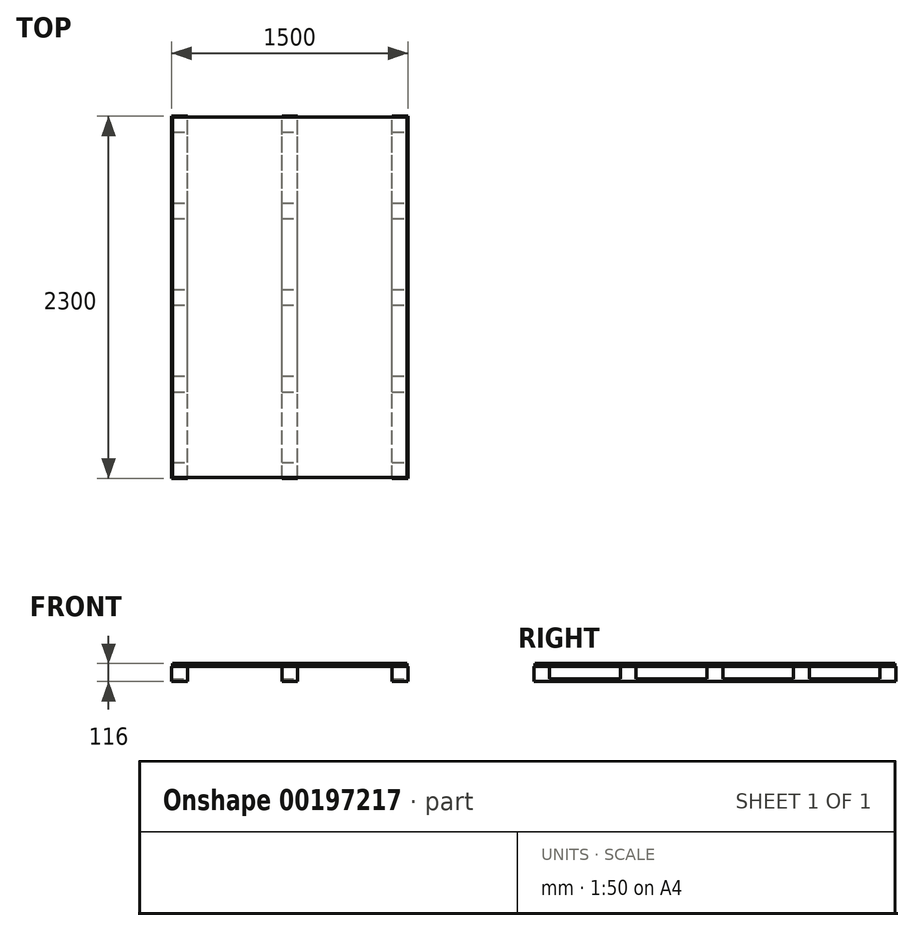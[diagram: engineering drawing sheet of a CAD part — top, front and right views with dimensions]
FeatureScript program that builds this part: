
annotation { "Feature Type Name" : "Feature", "Feature Type Description" : "" }
export const myFeature = defineFeature(function(context is Context, id is Id, definition is map)
    precondition{}
    {
        {
            var Q0;
            Q0=qCreatedBy(makeId("Top.planeOp"),FACE);
            var sketch = newSketch(context, id + "F0", { "sketchPlane" : qUnion([Q0])});
            skLineSegment(sketch, "E0.bottom", {"start": v(744, 1144) * mm, "end": v(-744, 1144) * mm});
            skLineSegment(sketch, "E0.top", {"start": v(744, -1144) * mm, "end": v(-744, -1144) * mm});
            skLineSegment(sketch, "E0.left", {"start": v(744, 1144) * mm, "end": v(744, -1144) * mm});
            skLineSegment(sketch, "E0.right", {"start": v(-744, 1144) * mm, "end": v(-744, -1144) * mm});
            skPoint(sketch, "E0.middle", {"position": v(0, 0) * mm});
            skSolve(sketch);
        }
        {
            var Q0;
            Q0=qSketchRegion(id+"F0",true);
            extrude(context, id + "F1", {"entities" : qUnion([Q0]), "depth" : 18 * mm});
        }
        {
            var Q0;
            Q0=makeQuery(id+"F1.opExtrude","CAP_FACE",FACE,{"disambiguationData":[OSD([sQuery(id+"F0.wireOp",EDGE,"E0.bottom"),sQuery(id+"F0.wireOp",EDGE,"E0.top"),sQuery(id+"F0.wireOp",EDGE,"E0.left"),sQuery(id+"F0.wireOp",EDGE,"E0.right")])],"isStart":true});
            var sketch = newSketch(context, id + "F2", { "sketchPlane" : qUnion([Q0])});
            skLineSegment(sketch, "E1.bottom", {"start": v(-750, 1150) * mm, "end": v(-650, 1150) * mm});
            skLineSegment(sketch, "E1.top", {"start": v(-750, 1050) * mm, "end": v(-650, 1050) * mm});
            skLineSegment(sketch, "E1.left", {"start": v(-750, 1150) * mm, "end": v(-750, 1050) * mm});
            skLineSegment(sketch, "E1.right", {"start": v(-650, 1150) * mm, "end": v(-650, 1050) * mm});
            skLineSegment(sketch, "E2.0.1.0", {"start": v(-750, 600) * mm, "end": v(-650, 600) * mm});
            skLineSegment(sketch, "E2.0.1.1", {"start": v(-650, 600) * mm, "end": v(-650, 500) * mm});
            skLineSegment(sketch, "E2.0.1.2", {"start": v(-750, 600) * mm, "end": v(-750, 500) * mm});
            skLineSegment(sketch, "E2.0.1.3", {"start": v(-750, 500) * mm, "end": v(-650, 500) * mm});
            skLineSegment(sketch, "E2.0.2.0", {"start": v(-750, 50) * mm, "end": v(-650, 50) * mm});
            skLineSegment(sketch, "E2.0.2.1", {"start": v(-650, 50) * mm, "end": v(-650, -50) * mm});
            skLineSegment(sketch, "E2.0.2.2", {"start": v(-750, 50) * mm, "end": v(-750, -50) * mm});
            skLineSegment(sketch, "E2.0.2.3", {"start": v(-750, -50) * mm, "end": v(-650, -50) * mm});
            skLineSegment(sketch, "E2.0.3.0", {"start": v(-750, -500) * mm, "end": v(-650, -500) * mm});
            skLineSegment(sketch, "E2.0.3.1", {"start": v(-650, -500) * mm, "end": v(-650, -600) * mm});
            skLineSegment(sketch, "E2.0.3.2", {"start": v(-750, -500) * mm, "end": v(-750, -600) * mm});
            skLineSegment(sketch, "E2.0.3.3", {"start": v(-750, -600) * mm, "end": v(-650, -600) * mm});
            skLineSegment(sketch, "E2.0.4.0", {"start": v(-750, -1050) * mm, "end": v(-650, -1050) * mm});
            skLineSegment(sketch, "E2.0.4.1", {"start": v(-650, -1050) * mm, "end": v(-650, -1150) * mm});
            skLineSegment(sketch, "E2.0.4.2", {"start": v(-750, -1050) * mm, "end": v(-750, -1150) * mm});
            skLineSegment(sketch, "E2.0.4.3", {"start": v(-750, -1150) * mm, "end": v(-650, -1150) * mm});
            skLineSegment(sketch, "E2.1.0.0", {"start": v(-50, 1150) * mm, "end": v(50, 1150) * mm});
            skLineSegment(sketch, "E2.1.0.1", {"start": v(50, 1150) * mm, "end": v(50, 1050) * mm});
            skLineSegment(sketch, "E2.1.0.2", {"start": v(-50, 1150) * mm, "end": v(-50, 1050) * mm});
            skLineSegment(sketch, "E2.1.0.3", {"start": v(-50, 1050) * mm, "end": v(50, 1050) * mm});
            skLineSegment(sketch, "E2.1.1.0", {"start": v(-50, 600) * mm, "end": v(50, 600) * mm});
            skLineSegment(sketch, "E2.1.1.1", {"start": v(50, 600) * mm, "end": v(50, 500) * mm});
            skLineSegment(sketch, "E2.1.1.2", {"start": v(-50, 600) * mm, "end": v(-50, 500) * mm});
            skLineSegment(sketch, "E2.1.1.3", {"start": v(-50, 500) * mm, "end": v(50, 500) * mm});
            skLineSegment(sketch, "E2.1.2.0", {"start": v(-50, 50) * mm, "end": v(50, 50) * mm});
            skLineSegment(sketch, "E2.1.2.1", {"start": v(50, 50) * mm, "end": v(50, -50) * mm});
            skLineSegment(sketch, "E2.1.2.2", {"start": v(-50, 50) * mm, "end": v(-50, -50) * mm});
            skLineSegment(sketch, "E2.1.2.3", {"start": v(-50, -50) * mm, "end": v(50, -50) * mm});
            skLineSegment(sketch, "E2.1.3.0", {"start": v(-50, -500) * mm, "end": v(50, -500) * mm});
            skLineSegment(sketch, "E2.1.3.1", {"start": v(50, -500) * mm, "end": v(50, -600) * mm});
            skLineSegment(sketch, "E2.1.3.2", {"start": v(-50, -500) * mm, "end": v(-50, -600) * mm});
            skLineSegment(sketch, "E2.1.3.3", {"start": v(-50, -600) * mm, "end": v(50, -600) * mm});
            skLineSegment(sketch, "E2.1.4.0", {"start": v(-50, -1050) * mm, "end": v(50, -1050) * mm});
            skLineSegment(sketch, "E2.1.4.1", {"start": v(50, -1050) * mm, "end": v(50, -1150) * mm});
            skLineSegment(sketch, "E2.1.4.2", {"start": v(-50, -1050) * mm, "end": v(-50, -1150) * mm});
            skLineSegment(sketch, "E2.1.4.3", {"start": v(-50, -1150) * mm, "end": v(50, -1150) * mm});
            skLineSegment(sketch, "E2.2.0.0", {"start": v(650, 1150) * mm, "end": v(750, 1150) * mm});
            skLineSegment(sketch, "E2.2.0.1", {"start": v(750, 1150) * mm, "end": v(750, 1050) * mm});
            skLineSegment(sketch, "E2.2.0.2", {"start": v(650, 1150) * mm, "end": v(650, 1050) * mm});
            skLineSegment(sketch, "E2.2.0.3", {"start": v(650, 1050) * mm, "end": v(750, 1050) * mm});
            skLineSegment(sketch, "E2.2.1.0", {"start": v(650, 600) * mm, "end": v(750, 600) * mm});
            skLineSegment(sketch, "E2.2.1.1", {"start": v(750, 600) * mm, "end": v(750, 500) * mm});
            skLineSegment(sketch, "E2.2.1.2", {"start": v(650, 600) * mm, "end": v(650, 500) * mm});
            skLineSegment(sketch, "E2.2.1.3", {"start": v(650, 500) * mm, "end": v(750, 500) * mm});
            skLineSegment(sketch, "E2.2.2.0", {"start": v(650, 50) * mm, "end": v(750, 50) * mm});
            skLineSegment(sketch, "E2.2.2.1", {"start": v(750, 50) * mm, "end": v(750, -50) * mm});
            skLineSegment(sketch, "E2.2.2.2", {"start": v(650, 50) * mm, "end": v(650, -50) * mm});
            skLineSegment(sketch, "E2.2.2.3", {"start": v(650, -50) * mm, "end": v(750, -50) * mm});
            skLineSegment(sketch, "E2.2.3.0", {"start": v(650, -500) * mm, "end": v(750, -500) * mm});
            skLineSegment(sketch, "E2.2.3.1", {"start": v(750, -500) * mm, "end": v(750, -600) * mm});
            skLineSegment(sketch, "E2.2.3.2", {"start": v(650, -500) * mm, "end": v(650, -600) * mm});
            skLineSegment(sketch, "E2.2.3.3", {"start": v(650, -600) * mm, "end": v(750, -600) * mm});
            skLineSegment(sketch, "E2.2.4.0", {"start": v(650, -1050) * mm, "end": v(750, -1050) * mm});
            skLineSegment(sketch, "E2.2.4.1", {"start": v(750, -1050) * mm, "end": v(750, -1150) * mm});
            skLineSegment(sketch, "E2.2.4.2", {"start": v(650, -1050) * mm, "end": v(650, -1150) * mm});
            skLineSegment(sketch, "E2.2.4.3", {"start": v(650, -1150) * mm, "end": v(750, -1150) * mm});
            skLineSegment(sketch, "E2.direction1", {"start": v(-750, 1150) * mm, "end": v(-50, 1150) * mm, "construction": true});
            skLineSegment(sketch, "E2.direction2", {"start": v(-750, 1150) * mm, "end": v(-750, 600) * mm, "construction": true});
            skSolve(sketch);
        }
        {
            var Q0;
            Q0=qSketchRegion(id+"F2",true);
            extrude(context, id + "F3", {"entities" : qUnion([Q0]), "operationType" : NewBodyOperationType.ADD, "depth" : 80 * mm});
        }
        {
            var Q0;
            Q0=makeQuery(id+"F3.opExtrude","CAP_FACE",FACE,{"disambiguationData":[OSD([sQuery(id+"F2.wireOp",EDGE,"E1.bottom"),sQuery(id+"F2.wireOp",EDGE,"E1.top"),sQuery(id+"F2.wireOp",EDGE,"E1.left"),sQuery(id+"F2.wireOp",EDGE,"E1.right")])],"isStart":false});
            var sketch = newSketch(context, id + "F4", { "sketchPlane" : qUnion([Q0])});
            skLineSegment(sketch, "E3.bottom", {"start": v(-750, 1150) * mm, "end": v(-650, 1150) * mm});
            skLineSegment(sketch, "E3.top", {"start": v(-750, -1150) * mm, "end": v(-650, -1150) * mm});
            skLineSegment(sketch, "E3.left", {"start": v(-750, 1150) * mm, "end": v(-750, -1150) * mm});
            skLineSegment(sketch, "E3.right", {"start": v(-650, 1150) * mm, "end": v(-650, -1150) * mm});
            skLineSegment(sketch, "E4.1.0.0", {"start": v(-50, 1150) * mm, "end": v(50, 1150) * mm});
            skLineSegment(sketch, "E4.1.0.1", {"start": v(-50, 1150) * mm, "end": v(-50, -1150) * mm});
            skLineSegment(sketch, "E4.1.0.2", {"start": v(50, 1150) * mm, "end": v(50, -1150) * mm});
            skLineSegment(sketch, "E4.1.0.3", {"start": v(-50, -1150) * mm, "end": v(50, -1150) * mm});
            skLineSegment(sketch, "E4.2.0.0", {"start": v(650, 1150) * mm, "end": v(750, 1150) * mm});
            skLineSegment(sketch, "E4.2.0.1", {"start": v(650, 1150) * mm, "end": v(650, -1150) * mm});
            skLineSegment(sketch, "E4.2.0.2", {"start": v(750, 1150) * mm, "end": v(750, -1150) * mm});
            skLineSegment(sketch, "E4.2.0.3", {"start": v(650, -1150) * mm, "end": v(750, -1150) * mm});
            skLineSegment(sketch, "E4.direction1", {"start": v(-750, 1150) * mm, "end": v(-50, 1150) * mm, "construction": true});
            skSolve(sketch);
        }
        {
            var Q0;
            Q0=qSketchRegion(id+"F4",true);
            extrude(context, id + "F5", {"entities" : qUnion([Q0]), "operationType" : NewBodyOperationType.ADD, "depth" : 18 * mm});
        }
    });
